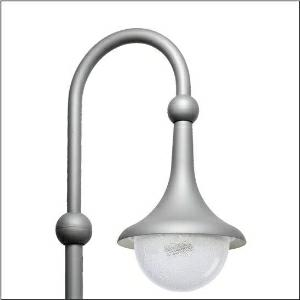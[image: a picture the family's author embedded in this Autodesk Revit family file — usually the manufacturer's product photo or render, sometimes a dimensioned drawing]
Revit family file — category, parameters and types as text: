
# Revit family: grosse_glocke___st1_2a_5xa1563k1b208_bcd9
name_source: partatom
category: Lighting Fixtures
units: mm (PartAtom-declared; Revit-internal decimal feet)

## family parameters
Cut with Voids When Loaded = No
Host = Face
Light Source = No
Part Type = Normal
Room Calculation Point = No
Round Connector Dimension = Use Diameter
Shared = No

## types (1)
- --- (1 x LED, 3380 lm, 23.4 W, 4000K)
    Apparent Load = 23 VA
    CIE Flux Codes = 29 66 94 99 100
    Color Rendering = 70
    Color Temperature = 4000K
    Default Elevation = 1800 mm
    Description = Large Bell, mast luminaire, primary light control with 3 zone facetted reflector, of plastic, silver coated, primary optical cover: enclosure, of PMMA, transparent structured, light distribution: ST1.2a, light emission: direct distribution, primary light characteristic: asymmetric, installation type: suspended mounting, LED, High Power LED, rated luminous flux: 3.380lm, luminous efficacy: 144lm/W, light colour: 740, colour temperature: 4000K, control gear: Plus, control: flexible luminous flux parameterisation, time-dependent luminous flux control, constant luminous flux control, digital communication interface, power reduction, electronic power reduction, mains connection: 230..240V, AC, 50/60Hz, start of lifetime: 23W, end of service life: 24W, reduction: 12W, luminaire housing, bell-shaped, of glass-fibre reinforced polyester, coated, Siteco® metallic grey (DB 702S), please order curved mast extension separately, diameter: 530mm, height: 695mm, mounting height: 4..6m, protection rating (complete): IP54, insulation class (complete): insulation class II (safety insulation), certification: CE, ENEC, VDE, impact resistance: IK08, standard-compliant lighting for roads and squares, packaging unit: 1 piece

Light Distribution: ST1.2a
    Height = 695 mm
    Lamp = 1 x LED
    Lamp Light Flux = 3380 lm
    Lamp Power = 23.4 W
    Lamp count = 1
    Length = 530 mm
    Luminous efficacy = 144 lm/W
    Manufacturer = Siteco
    ModVariant = No
    Model = 5XA1563K1B208
    Number of Poles = 1
    OnlyDefault = Yes
    Power Factor = 1
    Product Name = Große Glocke | ST1.2a
    Product group = mast luminaire | pylon annexe
    ProductGroupID = 6201
    Protection Class = Protection class II
    Protection Degree = IP 54
    RLX_Detail_Level = 1
    RLX_Emergency_Light_Flux = 0 lm
    RLX_Emergency_Type = 0
    RLX_Emergency_Type_DB = No
    RlxData = <blob elided: 54945 chars, md5=a7efc1ed>
    Socket = socket
    Standby Power = 0 W
    System Light Flux = 3380 lm
    System Power = 23 W
    Type Comments = factory setting: luminous flux: 100 % | dim-lin: 254 | 460 mA
    Type Image = l_1347684.jpg
    URL = http://relux.com
    VarID = @adj_197792
    Voltage = 0 V
    Weight = 0.00 kg
    Width = 0 mm  [stored 0 ft]

note: [stored X ft] marks values corroborated as IEEE doubles in the binary element streams (Revit-internal decimal feet)

## geometry (parser evidence)
native form markers: Blend x4, Sweep x10
no freeform markers — native parametric forms only
